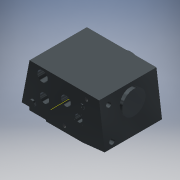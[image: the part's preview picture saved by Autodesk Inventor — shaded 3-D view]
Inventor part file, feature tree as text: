
AUTODESK INVENTOR PART (.ipt)
format: ipt  version: 2018 (Build 220112000, 112)  size: 368,128 bytes
history: native  units: in
note: dims shown in document units (in); Inventor stores cm internally (conversion verified against a paired STEP export)
features: extrude x23, sketch x21, other x3, fillet x2, thread x2, plane x2, hole x1, reference x1
ambient origin geometry x8: Origin, YZ Plane, XZ Plane, XY Plane, X Axis, Y Axis, Z Axis, Center Point
bodies: Solid1 (feature_tree)
feature tree (55):
  extrude  "Extrusion1"  Depth=10.4921in
  sketch  "Sketch3"  dims[d7=10.0in d8=0.5669in]
  extrude  "Extrusion2"  Depth=0.5669in
  extrude  "Extrusion3"  Depth=0.694in
  extrude  "Extrusion4"  Depth=0.7087in
  extrude  "Extrusion5"  Depth=0.0787in
  extrude  "Extrusion6"  Depth=13.4646in TaperAngle=0.0deg
  fillet  "Fillet1"  Radius=5.5118in
  fillet  "Fillet2"  Radius=6.2992in
  extrude  "Extrusion7"  Depth=2.7559in
  thread  "Thread1"  [1 undecoded]
  extrude  "Extrusion8"  Depth=1.1811in
  plane  "Work Plane3"
  extrude  "Extrusion10"  Depth=1.7717in
  extrude  "Extrusion11"  Depth=1.2106in
  extrude  "Extrusion12"  Depth=2.3622in TaperAngle=0.0deg
  extrude  "Extrusion13"  Depth=1.0236in TaperAngle=0.0deg
  extrude  "Extrusion14"  Depth=1.0236in TaperAngle=0.0deg
  hole  "Hole1"  [1 undecoded]
  extrude  "Extrusion15"  Depth=0.315in
  extrude  "Extrusion16"  Depth=0.0787in
  extrude  "Extrusion17"  Depth=0.7874in
  thread  "Thread2"  [1 undecoded]
  plane  "Work Plane2"
  extrude  "Extrusion18"  Depth=0.3937in TaperAngle=0.0deg
  extrude  "Extrusion19"  Depth=1.1811in
  extrude  "Extrusion20"  Depth=0.3937in
  sketch  "Sketch25"  dims[d105=0.3937in d106=0.0in d107=5.9055in]
  extrude  "Extrusion21"  TaperAngle=90.0deg  [1 undecoded]
  extrude  "Extrusion22"  Depth=2.7559in
  extrude  "Extrusion23"  Depth=7.4803in
  extrude  "Extrusion24"  TaperAngle=90.0deg  [1 undecoded]
  sketch  "Sketch1"  dims[d0=8.6614in d1=10.4921in]
  sketch  "Sketch4"  dims[d9=9.6457in d10=0.694in]
  sketch  "Sketch5"  dims[d11=1.7717in d12=0.7087in]
  sketch  "Sketch6"  dims[d14=16.3386in d15=0.0787in]
  sketch  "Sketch7"  dims[d16=0.0787in d17=13.4646in d18=0.0in d22=5.5118in d26=6.2992in]
  sketch  "Sketch8"  dims[d27=2.7559in d28=3.6024in d29=2.7559in]
  sketch  "Sketch10"  dims[d30=0.3937in d31=0.0in d34=1.1811in]
  sketch  "Sketch12"  dims[d37=1.7717in d38=2.0079in]
  sketch  "Sketch13"  dims[d39=1.2402in d42=1.2106in]
  sketch  "Sketch14"  dims[d43=1.8799in d44=2.3622in d45=0.0in]
  sketch  "Sketch16"  dims[d49=6.3386in d53=1.0236in d54=0.0in]
  sketch  "Sketch17"  dims[d55=2.2835in d56=1.0236in d57=0.0in]
  sketch  "Sketch19"  dims[d69=0.7874in d70=1.378in]
  sketch  "Sketch20"  dims[d72=0.3937in d73=0.315in]
  sketch  "Sketch21"  dims[d75=0.2362in d76=0.0in d77=0.0787in]
  other  "Work Axis1"
  sketch  "Sketch22"  dims[d78=0.0787in d82=0.7874in d83=1.1811in d84=0.0in]
  sketch  "Sketch23"  dims[d85=0.3937in d86=0.0in d91=0.3937in d92=0.0in]
  sketch  "Sketch24"  dims[d97=1.9685in d98=0.0in d103=1.1811in]
  sketch  "Sketch26"  dims[d108=5.9646in d109=90.0deg d110=2.7559in d111=7.4803in d112=90.0deg d113=0.3937in d114=0.0in d116=0.3937in d117=0.0in d118=2.9528in d120=3.2283in d121=1.1811in d122=0.1969in d123=0.0in d124=0.2559in d125=0.1181in d126=0.2362in d127=0.2559in d128=0.0787in d129=90.0deg d130=0.1969in d131=0.0in d132=6.6929in d133=90.0deg d134=1.7323in d135=2.4409in d136=0.7874in d137=0.0in d138=5.9055in d139=5.9646in d140=90.0deg d141=2.1654in d142=2.7559in d143=0.0in d144=0.9843in d145=1.3386in d146=0.7874in d147=0.7874in d148=0.0in d149=0.3937in d150=0.0in d151=0.0in d152=1.2992in d153=0.0in d154=17.3258in d155=0.0in d156=0.4331in d157=0.0in d160=0.1969in d163=0.1969in d164=0.1969in d165=0.5512in d166=0.0in d167=0.5512in d168=0.0in d169=0.5512in d170=0.0in d171=0.0394in d172=0.0in d173=4.0in d174=5.5118in d181=6.2205in d183=3.8189in]
  reference  "Reference1"
  other  "Lathe Model 2018.iam"
  other  "barrel:1"
note: 5 required parameter values undecoded (feature->parameter linkage not recoverable at this tier; creation-order binding heuristic only, values carry confidence <= 0.55)
